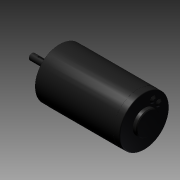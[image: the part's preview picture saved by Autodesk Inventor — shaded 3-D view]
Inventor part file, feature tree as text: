
AUTODESK INVENTOR PART (.ipt)
format: ipt  version: 2014 (Build 180170000, 170)  size: 138,752 bytes
history: native  units: in
note: dims shown in document units (in); Inventor stores cm internally (conversion verified against a paired STEP export)
features: chamfer x1, imported_body x1
ambient origin geometry x8: Origin, YZ Plane, XZ Plane, XY Plane, X Axis, Y Axis, Z Axis, Center Point
bodies: Body1 (feature_tree)
feature tree (2):
  chamfer  "Chamfer3"  [1 undecoded]
  imported_body  "Base1"
note: 1 required parameter value undecoded (feature->parameter linkage not recoverable at this tier; creation-order binding heuristic only, values carry confidence <= 0.55)
